# Revit family: LOROWERK 15199-050X
name_source: partatom
category: Sanitärinstallationen
revit_build: Autodesk Revit 2017 (Build: 20160225_1515(x64)
units: mm (PartAtom-declared; Revit-internal decimal feet)

## family parameters
Arbeitsebenenbasiert = Nein
Beim Laden mit Abzugskörper schneiden = Nein
Bemaßung runder Anschluss = Durchmesser verwenden
Gemeinsam genutzt = Nein
Immer vertikal = Ja
Raumberechnungspunkt = Nein
Teiletyp = Normal

## types (1)
- LOROWERK 15199-050X
    Anschluss an GLT, GA = Nein
    Beschreibung = LORO-X Speierrohr 250mm, Muffe, DN50
    Brandschutz mit Klasse R 120 nachrüstbar = Nein
    CONNECTOR0_DIAMETER_dZ_0r = 50 mm
    CONNECTOR0_dZ_00 = 247 mm
    CONNECTOR0_dZ_01 = 288 mm
    CONNECTOR0_ref_dZ = 247 mm
    CONNECTOR1_DIAMETER_dZ_0r = 50 mm
    CONNECTOR1_dZ_01 = 41 mm
    CONNECTOR1_ref_dZ = 41 mm
    DATANORM = 15199.050X
    Elektrischer Anschluss YesNo = Nein
    GTIN = 4038088096260
    HAN = 15199.050X
    HeinzeBIM = https://www.heinze.de
    Hersteller = LOROWERK K.H. Vahlbrauk GmbH & Co. KG
    Komplettartikel (Einteilig) aus Kombination (Mehrteileausführung) Ablaufgrundkörper und Aufsatzstück = Nein
    LOROWERK 15199.050X en Visibility = Ja
    Potenzialausgleich (Erdungsanschluss) vorhanden = Nein
    Produktfamilie = LORO-X Speierrohr 250mm, Muffe, DN50
    Produktklassifikation Text = Zubehoer
    Produktname = LORO-X Speierrohr 250mm, Muffe, DN50
    Typname = LORO-X Speierrohr 250mm, Muffe, DN50
    VDIBSN = 1000160000000000000000000000000000000000000000000100000000
